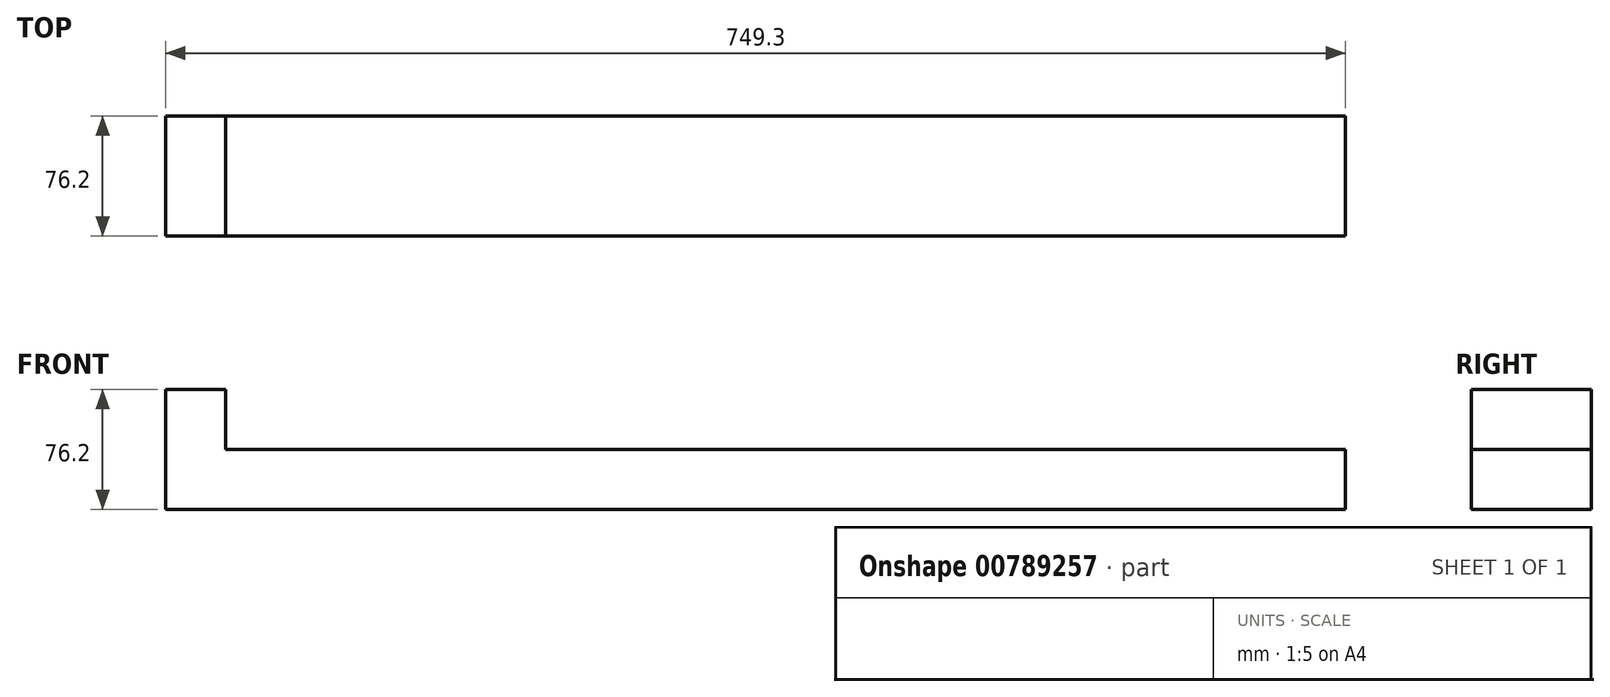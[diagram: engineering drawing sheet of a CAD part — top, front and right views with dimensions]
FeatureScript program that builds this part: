
annotation { "Feature Type Name" : "Feature", "Feature Type Description" : "" }
export const myFeature = defineFeature(function(context is Context, id is Id, definition is map)
    precondition{}
    {
        {
            var Q0;
            Q0=qCreatedBy(makeId("Front.planeOp"),FACE);
            var sketch = newSketch(context, id + "F0", { "sketchPlane" : qUnion([Q0])});
            skLineSegment(sketch, "E0", {"start": v(0, 0) * mm, "end": v(0, -76.2) * mm});
            skLineSegment(sketch, "E1", {"start": v(0, -76.2) * mm, "end": v(749.3, -76.2) * mm});
            skLineSegment(sketch, "E2", {"start": v(749.3, -76.2) * mm, "end": v(749.3, -38.1) * mm});
            skLineSegment(sketch, "E3", {"start": v(749.3, -38.1) * mm, "end": v(38.1, -38.1) * mm});
            skLineSegment(sketch, "E4", {"start": v(38.1, -38.1) * mm, "end": v(38.1, 0) * mm});
            skLineSegment(sketch, "E5", {"start": v(38.1, 0) * mm, "end": v(0, 0) * mm});
            skSolve(sketch);
        }
        {
            var Q0;
            Q0 = qSketchRegion(id + "F0", true);
            extrude(context, id + "F1", {"entities" : qUnion([Q0]), "endBound" : BoundingType.SYMMETRIC, "depth" : 76.2 * mm, "offsetDistance" : 25.4 * mm});
        }
    });
